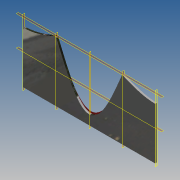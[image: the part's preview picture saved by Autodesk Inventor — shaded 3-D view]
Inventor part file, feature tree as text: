
AUTODESK INVENTOR PART (.ipt)
format: ipt  version: 2017.3 (Build 213257000, 257)  size: 194,048 bytes
history: native  units: in
note: dims shown in document units (in); Inventor stores cm internally (conversion verified against a paired STEP export)
features: plane x7, extrude x2, sketch x2, other x2
ambient origin geometry x8: Origin, YZ Plane, XZ Plane, XY Plane, X Axis, Y Axis, Z Axis, Center Point
bodies: Solid1 (feature_tree)
feature tree (13):
  extrude  "Extrusion1"  Depth=1.5in TaperAngle=0.0deg
  extrude  "Extrusion2"  Depth=0.001in TaperAngle=0.0deg
  plane  "Work Plane1 Centerline at surface"
  plane  "Work Plane2 Centerline at centerline"
  plane  "Work Plane3 Top"
  plane  "Work Plane4 Right"
  plane  "Work Plane5 Bottom"
  plane  "Work Plane6 Left"
  plane  "Work Plane7 Top"
  sketch  "Sketch1"  dims[d0=0.0in d1=43.5976in d2=1.5in d3=0.0in]
  other  "2D Equation Curve1"
  sketch  "Sketch2"  dims[d4=0.0in d5=43.5976in d6=0.001in d7=0.0in d8=-25.6245in d9=-50.55in d10=0.0in d11=-27.6845in d12=-55.369in d13=-83.0535in d14=0.0in]
  other  "2D Equation Curve2"
